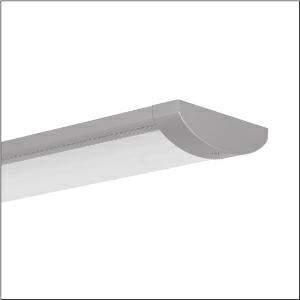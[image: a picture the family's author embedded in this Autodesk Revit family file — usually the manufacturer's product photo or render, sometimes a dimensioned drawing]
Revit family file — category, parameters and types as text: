
# Revit family: tv_20_5xa86174n0j
name_source: partatom
category: Lighting Fixtures
units: mm (PartAtom-declared; Revit-internal decimal feet)

## family parameters
Cut with Voids When Loaded = No
Host = Face
Light Source = No
Part Type = Normal
Room Calculation Point = No
Round Connector Dimension = Use Diameter
Shared = No

## types (1)
- TV 20 (1 x LED 4000K / CRI = 80 (unbekannt), 3960 lm, 4000K)
    Apparent Load = 37 VA
    CIE Flux Codes = 48 78 95 99 100
    Color Rendering = 80
    Color Temperature = 4000K
    Default Elevation = 1800 mm
    Description = TV 20, vandal-proof luminaire, primary light control with specular reflector, of aluminium, matt, primary optical cover: enclosure, of PC, frosted, light emission: direct distribution, primary light characteristic: symmetric, installation type: surface-mounted, LED, rated luminous flux: 3.960lm, luminous efficacy: 107lm/W, light colour: 840, colour temperature: 4000K, control gear: ECG, mains connection: 230V, AC, 50Hz, rated input power: 37W, luminaire housing, of aluminium, coated, Siteco® metallic grey (DB 702S), with wall and ceiling fixing element, length: 1.261mm, width: 260mm, height: 70mm, protection rating (complete): IP65, insulation class (complete): insulation class I (protective earthing), certification: CE, protection symbol: F, impact resistance: 2x IK10, standard: EN 60598, packaging unit: 1 piece
    Height = 70 mm
    Lamp = 1 x LED 4000K / CRI >= 80 (unbekannt)
    Lamp Light Flux = 3960 lm
    Lamp count = 1
    Length = 1261 mm
    Luminous efficacy = 107 lm/W
    Manufacturer = Siteco
    ModVariant = No
    Model = 5XA86174N0J
    Mounting Place = Ceiling
    Mounting Type = Surface mounted
    Number of Poles = 1
    OnlyDefault = Yes
    Power Factor = 1
    Product Name = TV 20
    Product group = vandal-proof luminaire
    ProductGroupID = 307
    Protection Class = Protection class I
    Protection Degree = IP 65
    RLX_Detail_Level = 1
    RLX_Emergency_Light_Flux = 0 lm
    RLX_Emergency_Type = 0
    RLX_Emergency_Type_DB = No
    RlxData = <blob elided: 25681 chars, md5=4482a42d>
    Socket = socket
    Standby Power = 0 W
    System Light Flux = 3960 lm
    System Power = 37 W
    Type Comments = Product without accessories
    Type Image = l_1004809.jpg
    URL = http://relux.com
    VarID = ---
    Voltage = 0 V
    Weight = 0.00 kg
    Width = 260 mm

## geometry (parser evidence)
native form markers: Blend x4, Sweep x11
no freeform markers — native parametric forms only
